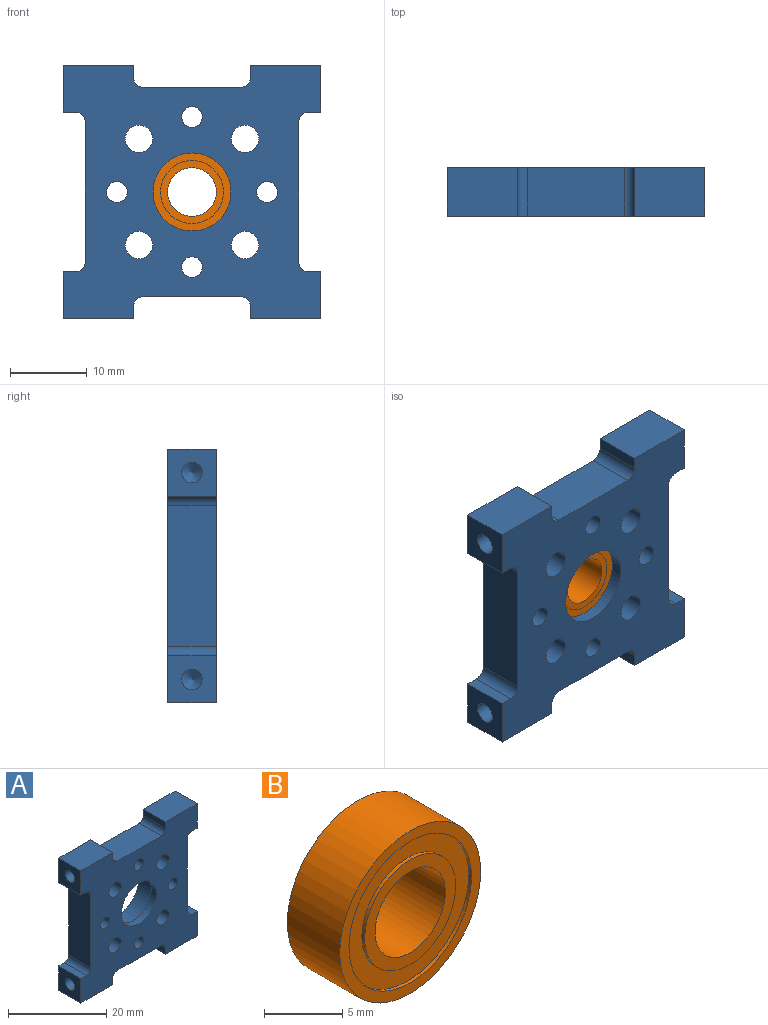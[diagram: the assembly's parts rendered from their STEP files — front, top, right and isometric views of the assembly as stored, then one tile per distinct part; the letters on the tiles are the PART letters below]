
ASSEMBLY  parts=2 mates=1
PART A: 49 faces, bbox 33.5x6.4x33 mm
  f0: cylinder r=1.78mm len=6.35mm, axis (0,1,0), area 70.9mm2, adj f18,f39
  f1: cylinder r=1.78mm len=6.35mm, axis (0,1,0), area 70.9mm2, adj f18,f39
  f2: cylinder r=1.78mm len=6.35mm, axis (0,1,0), area 70.9mm2, adj f18,f39
  f3: cylinder r=1.35mm len=6.35mm, axis (0,1,0), area 54mm2, adj f18,f39
  f4: cylinder r=1.35mm len=6.35mm, axis (0,1,0), area 54mm2, adj f18,f39
  f5: cylinder r=1.35mm len=6.35mm, axis (0,1,0), area 54mm2, adj f18,f39
  f6: cylinder r=5.08mm len=10.16mm, axis (0,1,0), area 50.3mm2, adj f18,f40
  f7: cylinder r=6.35mm len=12.7mm, axis (0,1,0), area 190.5mm2, adj f39,f40
  f8: cylinder r=1.78mm len=6.35mm, axis (0,1,0), area 70.9mm2, adj f18,f39
  f9: cylinder r=1.35mm len=6.35mm, axis (0,1,0), area 54mm2, adj f18,f39
  f10: cylinder r=1.35mm len=7.62mm, axis (1,0,0), area 64.8mm2, adj f11,f35
  f11: cone r=1.35mm half-angle=59deg, axis (1,0,0), area 6.7mm2, adj f10
  f12: cylinder r=1.35mm len=7.62mm, axis (1,0,0), area 64.8mm2, adj f13,f19
  f13: cone r=1.35mm half-angle=59deg, axis (1,0,0), area 6.7mm2, adj f12
  f14: cylinder r=1.35mm len=7.62mm, axis (-1,0,0), area 64.8mm2, adj f15,f29
  f15: cone r=1.35mm half-angle=59deg, axis (-1,0,0), area 6.7mm2, adj f14
  f16: cylinder r=1.35mm len=7.62mm, axis (-1,0,0), area 64.8mm2, adj f17,f25
  f17: cone r=1.35mm half-angle=59deg, axis (-1,0,0), area 6.7mm2, adj f16
  f18: plane 33.53x33.02mm, normal (0,-1,0), area 759.7mm2, adj f0,f1,f2,f3,f4,f5,f6,f8
  f19: plane 6.35x6.1mm, normal (1,0,0), area 33mm2, adj f12,f18,f20,f38,f39
  f20: plane 9.14x6.35mm, normal (0,0,-1), area 58.1mm2, adj f18,f19,f21,f39
  f21: plane 6.35x1.6mm, normal (-1,0,0), area 10.1mm2, adj f18,f20,f39,f47
  f22: plane 12.7x6.35mm, normal (0,0,-1), area 80.6mm2, adj f18,f39,f46,f47
  f23: plane 6.35x1.6mm, normal (1,0,0), area 10.1mm2, adj f18,f24,f39,f46
  f24: plane 9.14x6.35mm, normal (0,0,-1), area 58.1mm2, adj f18,f23,f25,f39
  f25: plane 6.35x6.1mm, normal (-1,0,0), area 33mm2, adj f16,f18,f24,f26,f39
  f26: plane 6.35x1.59mm, normal (0,0,1), area 10.1mm2, adj f18,f25,f39,f48
  f27: plane 18.29x6.35mm, normal (-1,0,0), area 116.1mm2, adj f18,f39,f45,f48
  f28: plane 6.35x1.59mm, normal (0,0,-1), area 10.1mm2, adj f18,f29,f39,f45
  f29: plane 6.35x6.1mm, normal (-1,0,0), area 33mm2, adj f14,f18,f28,f30,f39
  f30: plane 9.14x6.35mm, normal (0,0,1), area 58.1mm2, adj f18,f29,f31,f39
  f31: plane 6.35x1.6mm, normal (1,0,0), area 10.1mm2, adj f18,f30,f39,f44
  f32: plane 12.7x6.35mm, normal (0,0,1), area 80.6mm2, adj f18,f39,f43,f44
  f33: plane 6.35x1.6mm, normal (-1,0,0), area 10.1mm2, adj f18,f34,f39,f43
  f34: plane 9.14x6.35mm, normal (0,0,1), area 58.1mm2, adj f18,f33,f35,f39
  f35: plane 6.35x6.1mm, normal (1,0,0), area 33mm2, adj f10,f18,f34,f36,f39
  f36: plane 6.35x1.59mm, normal (0,0,-1), area 10.1mm2, adj f18,f35,f39,f42
  f37: plane 18.29x6.35mm, normal (1,0,0), area 116.1mm2, adj f18,f39,f41,f42
  f38: plane 6.35x1.59mm, normal (0,0,1), area 10.1mm2, adj f18,f19,f39,f41
  f39: plane 33.53x33.02mm, normal (0,1,0), area 714.1mm2, adj f0,f1,f2,f3,f4,f5,f7,f8
  f40: plane 12.7x12.7mm, normal (0,1,0), area 45.6mm2, adj f6,f7
  f41: cylinder r=1.27mm len=6.35mm, axis (0,1,0), area 12.7mm2, adj f18,f37,f38,f39
  f42: cylinder r=1.27mm len=6.35mm, axis (0,1,0), area 12.7mm2, adj f18,f36,f37,f39
  f43: cylinder r=1.27mm len=6.35mm, axis (0,1,0), area 12.7mm2, adj f18,f32,f33,f39
  f44: cylinder r=1.27mm len=6.35mm, axis (0,1,0), area 12.7mm2, adj f18,f31,f32,f39
  f45: cylinder r=1.27mm len=6.35mm, axis (0,1,0), area 12.7mm2, adj f18,f27,f28,f39
  f46: cylinder r=1.27mm len=6.35mm, axis (0,1,0), area 12.7mm2, adj f18,f22,f23,f39
  f47: cylinder r=1.27mm len=6.35mm, axis (0,1,0), area 12.7mm2, adj f18,f21,f22,f39
  f48: cylinder r=1.27mm len=6.35mm, axis (0,1,0), area 12.7mm2, adj f18,f26,f27,f39
PART B: 12 faces, bbox 12.7x4.7x12.7 mm
  f0: cylinder r=4.1mm len=8.2mm, axis (0,-1,0), area 6.5mm2, adj f6,f11
  f1: cylinder r=5.52mm len=11.05mm, axis (0,-1,0), area 8.8mm2, adj f9,f11
  f2: cylinder r=4.1mm len=8.2mm, axis (0,1,0), area 6.5mm2, adj f7,f10
  f3: cylinder r=5.52mm len=11.05mm, axis (0,1,0), area 8.8mm2, adj f8,f10
  f4: cylinder r=3.17mm len=6.35mm, axis (0,-1,0), area 94.2mm2, adj f6,f7
  f5: cylinder r=6.35mm len=12.7mm, axis (0,-1,0), area 188.5mm2, adj f8,f9
  f6: plane 8.2x8.2mm, normal (0,-1,0), area 21.2mm2, adj f0,f4
  f7: plane 8.2x8.2mm, normal (0,1,0), area 21.2mm2, adj f2,f4
  f8: plane 12.7x12.7mm, normal (0,1,0), area 30.8mm2, adj f3,f5
  f9: plane 12.7x12.7mm, normal (0,-1,0), area 30.8mm2, adj f1,f5
  f10: plane 11.05x11.05mm, normal (0,1,0), area 43mm2, adj f2,f3
  f11: plane 11.05x11.05mm, normal (0,-1,0), area 43mm2, adj f0,f1
PLACE A t=(7.62,14.22,28.39)mm
PLACE B t=(7.62,15.79,28.39)mm
MATE fastened B.f0 <-> A.f6  axis (0,1,0) through (7.62,15.79,28.39)mm
